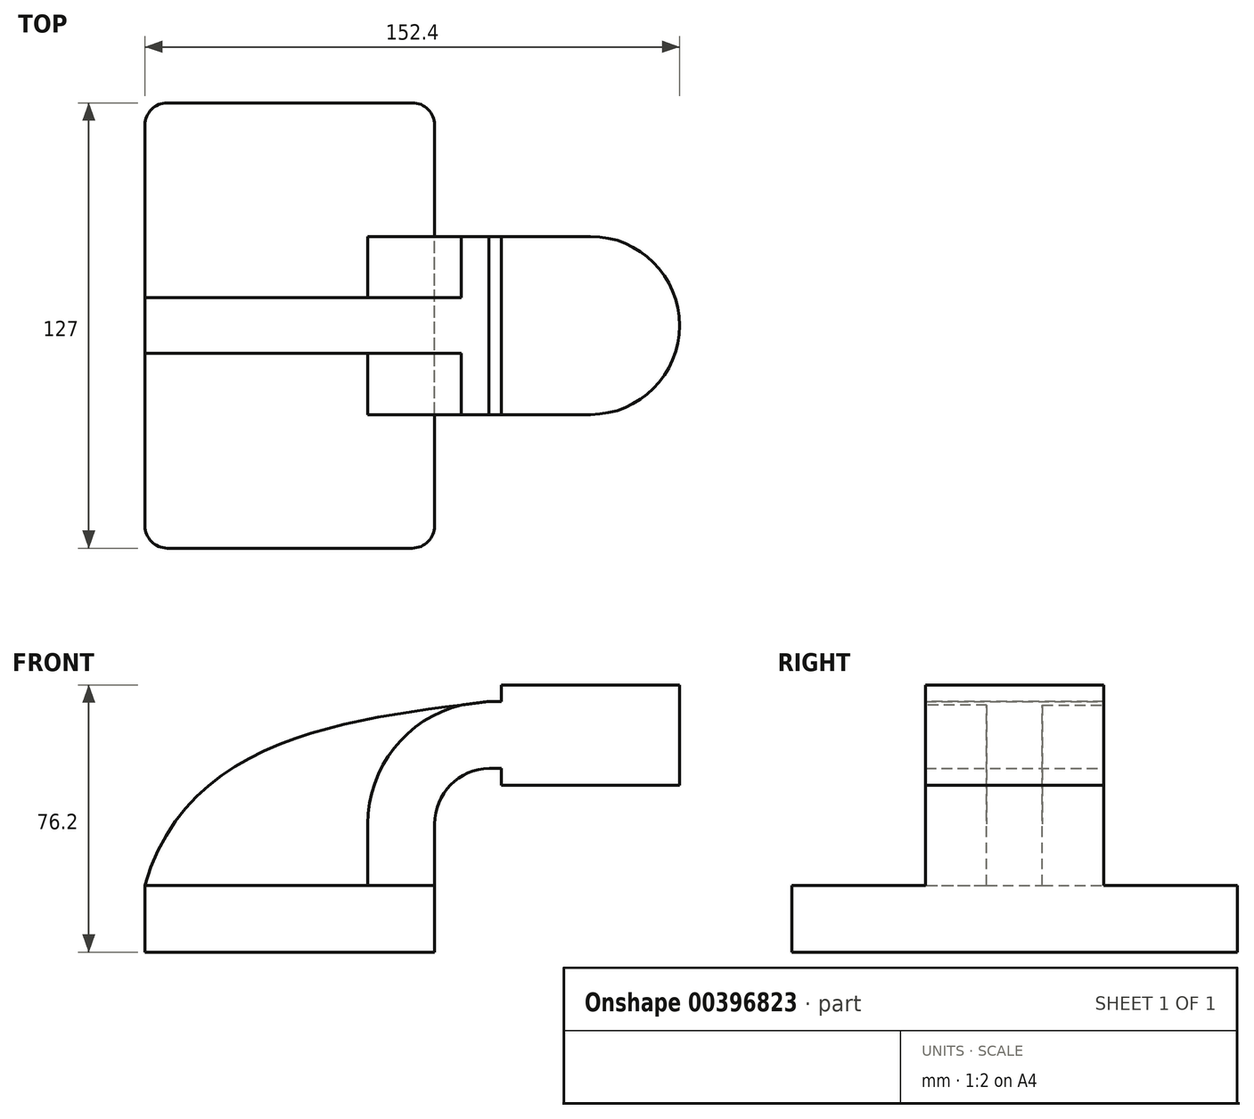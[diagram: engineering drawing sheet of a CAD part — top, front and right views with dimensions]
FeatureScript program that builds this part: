
annotation { "Feature Type Name" : "Feature", "Feature Type Description" : "" }
export const myFeature = defineFeature(function(context is Context, id is Id, definition is map)
    precondition{}
    {
        {
            var Q0;
            Q0=qCreatedBy(makeId("Front.planeOp"),FACE);
            var sketch = newSketch(context, id + "F0", { "sketchPlane" : qUnion([Q0])});
            skLineSegment(sketch, "E0.bottom", {"start": v(41.28, 9.53) * mm, "end": v(-41.28, 9.53) * mm});
            skLineSegment(sketch, "E0.top", {"start": v(41.28, -9.52) * mm, "end": v(-41.28, -9.52) * mm});
            skLineSegment(sketch, "E0.left", {"start": v(41.28, 9.53) * mm, "end": v(41.28, -9.52) * mm});
            skLineSegment(sketch, "E0.right", {"start": v(-41.28, 9.53) * mm, "end": v(-41.28, -9.52) * mm});
            skPoint(sketch, "E0.middle", {"position": v(0, 0) * mm});
            skLineSegment(sketch, "E1.bottom", {"start": v(111.12, 38.1) * mm, "end": v(60.33, 38.1) * mm});
            skLineSegment(sketch, "E1.top", {"start": v(111.12, 66.68) * mm, "end": v(60.33, 66.68) * mm});
            skLineSegment(sketch, "E1.left", {"start": v(111.12, 38.1) * mm, "end": v(111.12, 66.68) * mm});
            skLineSegment(sketch, "E1.right", {"start": v(60.33, 38.1) * mm, "end": v(60.33, 66.67) * mm});
            skPoint(sketch, "E1.middle", {"position": v(85.72, 52.39) * mm});
            skLineSegment(sketch, "E2", {"start": v(41.28, 9.53) * mm, "end": v(41.28, 27) * mm});
            skArc(sketch, "E3", {"start": v(41.27, 27) * mm, "mid": v(45.83, 38.13) * mm, "end": v(56.87, 42.88) * mm});
            skLineSegment(sketch, "E4", {"start": v(56.87, 42.88) * mm, "end": v(79.88, 42.88) * mm});
            skLineSegment(sketch, "E5.0", {"start": v(56.73, 61.93) * mm, "end": v(79.88, 61.93) * mm});
            skArc(sketch, "E5.1", {"start": v(22.23, 27) * mm, "mid": v(32.3, 51.55) * mm, "end": v(56.73, 61.93) * mm});
            skLineSegment(sketch, "E5.2", {"start": v(22.22, 9.53) * mm, "end": v(22.22, 27) * mm});
            skFitSpline(sketch, "E6", {"points": [v(-41.28, 9.53) * mm, v(56.73, 61.93) * mm], "startDerivative": vector(37.1, 130.54) * mm, "endDerivative": vector(109.97, 13.98) * mm});
            skLineSegment(sketch, "E7", {"start": v(85.72, 66.68) * mm, "end": v(85.72, 38.1) * mm});
            skSolve(sketch);
        }
        {
            var Q0;
            Q0=makeQuery(id+"F0.imprint","IMPRINT",FACE,{"disambiguationData":[TD([[makeQuery(id+"F0.imprint","IMPRINT",EDGE,{"derivedFrom":sQuery(id+"F0.wireOp",EDGE,"E0.top")}),-1.0]])]});
            extrude(context, id + "F1", {"entities" : qUnion([Q0]), "endBound" : BoundingType.SYMMETRIC, "depth" : 127 * mm});
        }
        {
            var Q0;
            {var subQ1=sQuery(id+"F0.wireOp",EDGE,"E2");Q0=makeQuery(id+"F0.imprint","IMPRINT",FACE,{"disambiguationData":[TD([[makeQuery(id+"F0.imprint","IMPRINT",EDGE,{"derivedFrom":subQ1}),1.0]])]});}
            var Q1;
            {var subQ6=sQuery(id+"F0.wireOp",EDGE,"E7");Q1=makeQuery(id+"F0.imprint","IMPRINT",FACE,{"disambiguationData":[TD([[makeQuery(id+"F0.imprint","IMPRINT",EDGE,{"derivedFrom":subQ6}),-1.0]])]});}
            extrude(context, id + "F2", {"entities" : qUnion([Q0, Q1]), "operationType" : NewBodyOperationType.ADD, "endBound" : BoundingType.SYMMETRIC, "depth" : 50.8 * mm});
        }
        {
            var Q0;
            {var subQ3=sQuery(id+"F0.wireOp",EDGE,"E5.2");Q0=makeQuery(id+"F0.imprint","IMPRINT",FACE,{"disambiguationData":[TD([[makeQuery(id+"F0.imprint","IMPRINT",EDGE,{"derivedFrom":subQ3}),1.0]])]});}
            extrude(context, id + "F3", {"entities" : qUnion([Q0]), "operationType" : NewBodyOperationType.ADD, "endBound" : BoundingType.SYMMETRIC, "depth" : 15.88 * mm});
        }
        {
            var Q0;
            {var subQ0=sQuery(id+"F0.wireOp",EDGE,"E1.left");Q0=makeQuery(id+"F0.imprint","IMPRINT",FACE,{"disambiguationData":[TD([[makeQuery(id+"F0.imprint","IMPRINT",EDGE,{"derivedFrom":subQ0}),1.0]])]});}
            var Q1;
            Q1=sQuery(id+"F0.wireOp",EDGE,"E7");
            revolve(context, id + "F4", {"operationType" : NewBodyOperationType.ADD, "entities" : qUnion([Q0]), "axis" : qUnion([Q1]), "revolveType" : RevolveType.FULL});
        }
        {
            var Q0;
            Q0=makeQuery(id+"F1.opExtrude","CAP_EDGE",EDGE,{"disambiguationData":[OSD([sQuery(id+"F0.wireOp",EDGE,"E0.right")])],"isStart":false});
            var Q1;
            Q1=makeQuery(id+"F1.opExtrude","CAP_EDGE",EDGE,{"disambiguationData":[OSD([sQuery(id+"F0.wireOp",EDGE,"E0.left")])],"isStart":false});
            var Q2;
            Q2=makeQuery(id+"F1.opExtrude","CAP_EDGE",EDGE,{"disambiguationData":[OSD([sQuery(id+"F0.wireOp",EDGE,"E0.left")])],"isStart":true});
            var Q3;
            Q3=makeQuery(id+"F1.opExtrude","CAP_EDGE",EDGE,{"disambiguationData":[OSD([sQuery(id+"F0.wireOp",EDGE,"E0.right")])],"isStart":true});
            fillet(context, id + "F5", {"entities" : qUnion([Q0, Q1, Q2, Q3]), "radius" : 6.35 * mm, "tangentPropagation" : true, "allowEdgeOverflow" : false});
        }
    });
